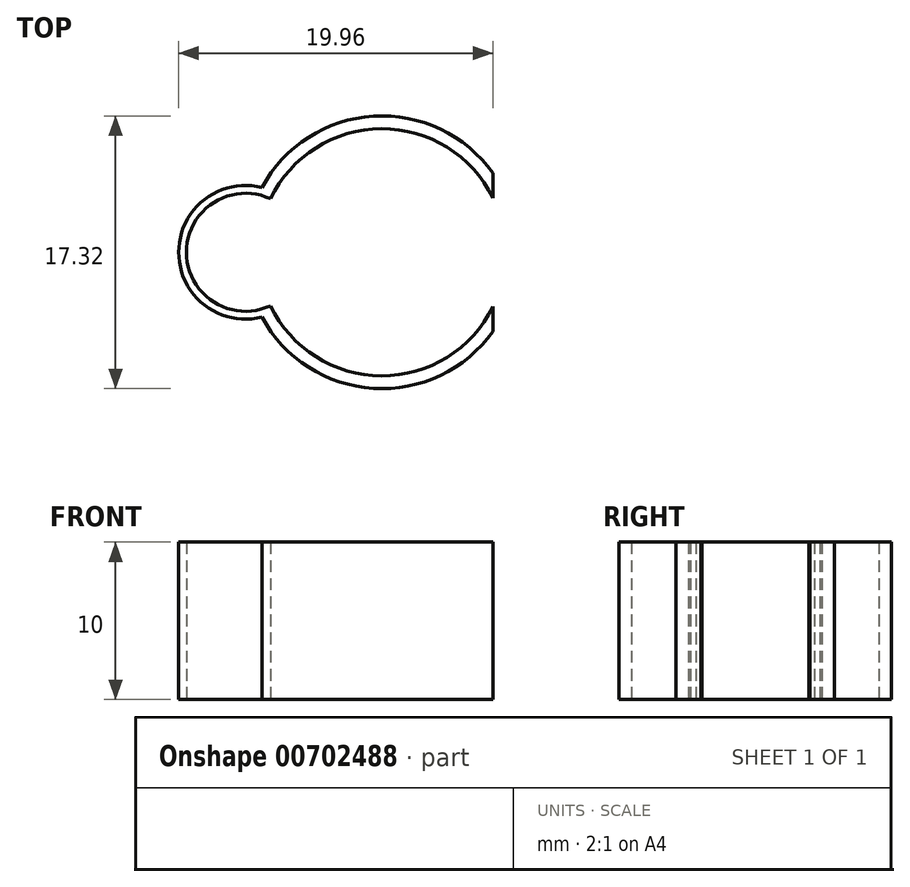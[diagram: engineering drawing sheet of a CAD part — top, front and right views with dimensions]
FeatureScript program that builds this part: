
annotation { "Feature Type Name" : "Feature", "Feature Type Description" : "" }
export const myFeature = defineFeature(function(context is Context, id is Id, definition is map)
    precondition{}
    {
        {
            var Q0;
            Q0=qCreatedBy(makeId("Top.planeOp"),FACE);
            var sketch = newSketch(context, id + "F0", { "sketchPlane" : qUnion([Q0])});
            skCircle(sketch, "E0", {"center": v(0, 0) * mm, "radius": 7.85 * mm});
            skCircle(sketch, "E1", {"center": v(0, 0) * mm, "radius": 8.66 * mm});
            skCircle(sketch, "E2", {"center": v(-8.66, 0) * mm, "radius": 3.75 * mm});
            skCircle(sketch, "E3", {"center": v(-8.66, 0) * mm, "radius": 4.25 * mm});
            skLineSegment(sketch, "E4", {"start": v(7.05, 5.03) * mm, "end": v(7.05, 3.46) * mm});
            skLineSegment(sketch, "E5", {"start": v(7.05, -3.46) * mm, "end": v(7.05, -5.03) * mm});
            skSolve(sketch);
        }
        {
            var Q0;
            {var subQ0=sQuery(id+"F0.wireOp",EDGE,"b5i4uvnI-YS7I-iQm8-zbXG-z9BTK1NYs2xS");Q0=makeQuery(id+"F0.imprint","IMPRINT",FACE,{"disambiguationData":[TD([[makeQuery(id+"F0.imprint","IMPRINT",EDGE,{"derivedFrom":subQ0}),-1.0]])]});}
            var Q1;
            {var subQ0=sQuery(id+"F0.wireOp",EDGE,"E3");var subQ1=sQuery(id+"F0.wireOp",EDGE,"E0");var subQ2=makeQuery(id+"F0.imprint","INTERSECT",VERTEX,{"disambiguationData":[OD(0.0)],"derivedFrom":[subQ1,subQ0]});Q1=makeQuery(id+"F0.imprint","IMPRINT",FACE,{"disambiguationData":[TD([[makeQuery(id+"F0.imprint","IMPRINT",EDGE,{"disambiguationData":[TD([[subQ2,-1.0]])],"derivedFrom":subQ1}),-1.0]])]});}
            var Q2;
            {var subQ0=sQuery(id+"F0.wireOp",EDGE,"MbiijEaS-GBBS-EwlK-B2ir-NtHmAoSLFiy8");Q2=makeQuery(id+"F0.imprint","IMPRINT",FACE,{"disambiguationData":[TD([[makeQuery(id+"F0.imprint","IMPRINT",EDGE,{"derivedFrom":subQ0}),-1.0]])]});}
            var Q3;
            {var subQ0=sQuery(id+"F0.wireOp",EDGE,"E2");var subQ1=sQuery(id+"F0.wireOp",EDGE,"E0");var subQ2=makeQuery(id+"F0.imprint","INTERSECT",VERTEX,{"disambiguationData":[OD(1.0)],"derivedFrom":[subQ1,subQ0]});Q3=makeQuery(id+"F0.imprint","IMPRINT",FACE,{"disambiguationData":[TD([[makeQuery(id+"F0.imprint","IMPRINT",EDGE,{"disambiguationData":[TD([[subQ2,-1.0]])],"derivedFrom":subQ1}),-1.0]])]});}
            var Q4;
            {var subQ0=sQuery(id+"F0.wireOp",EDGE,"E3");var subQ1=sQuery(id+"F0.wireOp",EDGE,"E1");var subQ2=makeQuery(id+"F0.imprint","INTERSECT",VERTEX,{"disambiguationData":[OD(0.0)],"derivedFrom":[subQ1,subQ0]});Q4=makeQuery(id+"F0.imprint","IMPRINT",FACE,{"disambiguationData":[TD([[makeQuery(id+"F0.imprint","IMPRINT",EDGE,{"disambiguationData":[TD([[subQ2,-1.0]])],"derivedFrom":subQ1}),-1.0]])]});}
            extrude(context, id + "F1", {"entities" : qUnion([Q0, Q1, Q2, Q3, Q4]), "depth" : 10 * mm, "offsetDistance" : 25 * mm});
        }
        {
            var Q0;
            Q0=makeQuery(id+"F1.opExtrude","SWEPT_BODY",BODY,{"disambiguationData":[OSD([sQuery(id+"F0.wireOp",EDGE,"E0"),sQuery(id+"F0.wireOp",EDGE,"E1"),sQuery(id+"F0.wireOp",EDGE,"E2"),sQuery(id+"F0.wireOp",EDGE,"E3"),sQuery(id+"F0.wireOp",EDGE,"b5i4uvnI-YS7I-iQm8-zbXG-z9BTK1NYs2xS"),sQuery(id+"F0.wireOp",EDGE,"MbiijEaS-GBBS-EwlK-B2ir-NtHmAoSLFiy8")])]});
            transform(context, id + "F2", {"entities" : qUnion([Q0]), "transformType" : TransformType.TRANSLATION_3D, "dx" : -14.3 * mm, "dy" : 0 * mm, "dz" : 0 * mm, "makeCopy" : true});
        }
        {
            var Q0;
            Q0=makeQuery(id+"F2.opPattern","COPY",BODY,{"derivedFrom":makeQuery(id+"F1.opExtrude","SWEPT_BODY",BODY,{"disambiguationData":[OSD([sQuery(id+"F0.wireOp",EDGE,"E0"),sQuery(id+"F0.wireOp",EDGE,"E1"),sQuery(id+"F0.wireOp",EDGE,"E2"),sQuery(id+"F0.wireOp",EDGE,"E3"),sQuery(id+"F0.wireOp",EDGE,"b5i4uvnI-YS7I-iQm8-zbXG-z9BTK1NYs2xS"),sQuery(id+"F0.wireOp",EDGE,"MbiijEaS-GBBS-EwlK-B2ir-NtHmAoSLFiy8")])]}),"instanceName":"1"});
            transform(context, id + "F3", {"entities" : qUnion([Q0]), "transformType" : TransformType.TRANSLATION_3D, "dx" : -13 * mm, "dy" : 0 * mm, "dz" : 0 * mm, "makeCopy" : true});
        }
        {
            var Q0;
            Q0=makeQuery(id+"F3.opPattern","COPY",BODY,{"derivedFrom":makeQuery(id+"F2.opPattern","COPY",BODY,{"derivedFrom":makeQuery(id+"F1.opExtrude","SWEPT_BODY",BODY,{"disambiguationData":[OSD([sQuery(id+"F0.wireOp",EDGE,"E0"),sQuery(id+"F0.wireOp",EDGE,"E1"),sQuery(id+"F0.wireOp",EDGE,"E2"),sQuery(id+"F0.wireOp",EDGE,"E3"),sQuery(id+"F0.wireOp",EDGE,"b5i4uvnI-YS7I-iQm8-zbXG-z9BTK1NYs2xS"),sQuery(id+"F0.wireOp",EDGE,"MbiijEaS-GBBS-EwlK-B2ir-NtHmAoSLFiy8")])]}),"instanceName":"1"}),"instanceName":"1"});
            deleteBodies(context, id + "F4", {"entities" : qUnion([Q0])});
        }
        {
            var Q0;
            Q0=makeQuery(id+"F2.opPattern","COPY",BODY,{"derivedFrom":makeQuery(id+"F1.opExtrude","SWEPT_BODY",BODY,{"disambiguationData":[OSD([sQuery(id+"F0.wireOp",EDGE,"E0"),sQuery(id+"F0.wireOp",EDGE,"E1"),sQuery(id+"F0.wireOp",EDGE,"E2"),sQuery(id+"F0.wireOp",EDGE,"E3"),sQuery(id+"F0.wireOp",EDGE,"b5i4uvnI-YS7I-iQm8-zbXG-z9BTK1NYs2xS"),sQuery(id+"F0.wireOp",EDGE,"MbiijEaS-GBBS-EwlK-B2ir-NtHmAoSLFiy8")])]}),"instanceName":"1"});
            deleteBodies(context, id + "F5", {"entities" : qUnion([Q0])});
        }
        {
            var Q0;
            {var subQ0=sQuery(id+"F0.wireOp",EDGE,"E4");Q0=makeQuery(id+"F0.imprint","IMPRINT",FACE,{"disambiguationData":[TD([[makeQuery(id+"F0.imprint","IMPRINT",EDGE,{"derivedFrom":subQ0}),-1.0]])]});}
            var Q1;
            {var subQ0=sQuery(id+"F0.wireOp",EDGE,"E5");Q1=makeQuery(id+"F0.imprint","IMPRINT",FACE,{"disambiguationData":[TD([[makeQuery(id+"F0.imprint","IMPRINT",EDGE,{"derivedFrom":subQ0}),-1.0]])]});}
            var Q2;
            {var subQ0=sQuery(id+"F0.wireOp",EDGE,"E3");var subQ1=sQuery(id+"F0.wireOp",EDGE,"E0");var subQ2=makeQuery(id+"F0.imprint","INTERSECT",VERTEX,{"disambiguationData":[OD(0.0)],"derivedFrom":[subQ1,subQ0]});Q2=makeQuery(id+"F0.imprint","IMPRINT",FACE,{"disambiguationData":[TD([[makeQuery(id+"F0.imprint","IMPRINT",EDGE,{"disambiguationData":[TD([[subQ2,-1.0]])],"derivedFrom":subQ1}),-1.0]])]});}
            var Q3;
            {var subQ0=sQuery(id+"F0.wireOp",EDGE,"E2");var subQ1=sQuery(id+"F0.wireOp",EDGE,"E0");var subQ2=makeQuery(id+"F0.imprint","INTERSECT",VERTEX,{"disambiguationData":[OD(1.0)],"derivedFrom":[subQ1,subQ0]});Q3=makeQuery(id+"F0.imprint","IMPRINT",FACE,{"disambiguationData":[TD([[makeQuery(id+"F0.imprint","IMPRINT",EDGE,{"disambiguationData":[TD([[subQ2,-1.0]])],"derivedFrom":subQ1}),-1.0]])]});}
            extrude(context, id + "F6", {"entities" : qUnion([Q0, Q1, Q2, Q3]), "operationType" : NewBodyOperationType.ADD, "depth" : 10 * mm, "offsetDistance" : 25 * mm});
        }
        {
            var Q0;
            Q0=makeQuery(id+"F1.opExtrude","SWEPT_BODY",BODY,{"disambiguationData":[OSD([sQuery(id+"F0.wireOp",EDGE,"E0"),sQuery(id+"F0.wireOp",EDGE,"E2"),sQuery(id+"F0.wireOp",EDGE,"E3")])]});
            transform(context, id + "F7", {"entities" : qUnion([Q0]), "transformType" : TransformType.TRANSLATION_3D, "dx" : -22.5 * mm, "dy" : 0 * mm, "dz" : 0 * mm, "makeCopy" : true});
        }
        {
            var Q0;
            Q0=makeQuery(id+"F1.opExtrude","SWEPT_BODY",BODY,{"disambiguationData":[OSD([sQuery(id+"F0.wireOp",EDGE,"E0"),sQuery(id+"F0.wireOp",EDGE,"E2"),sQuery(id+"F0.wireOp",EDGE,"E3")])]});
            transform(context, id + "F8", {"entities" : qUnion([Q0]), "transformType" : TransformType.TRANSLATION_3D, "dx" : 0 * mm, "dy" : 18.6 * mm, "dz" : 0 * mm, "makeCopy" : true});
        }
        {
            var Q0;
            Q0=makeQuery(id+"F7.opPattern","COPY",BODY,{"derivedFrom":makeQuery(id+"F1.opExtrude","SWEPT_BODY",BODY,{"disambiguationData":[OSD([sQuery(id+"F0.wireOp",EDGE,"E0"),sQuery(id+"F0.wireOp",EDGE,"E2"),sQuery(id+"F0.wireOp",EDGE,"E3")])]}),"instanceName":"1"});
            transform(context, id + "F9", {"entities" : qUnion([Q0]), "transformType" : TransformType.TRANSLATION_3D, "dx" : 0 * mm, "dy" : 20.1 * mm, "dz" : 0 * mm, "makeCopy" : true});
        }
        {
            var Q0;
            Q0=makeQuery(id+"F7.opPattern","COPY",BODY,{"derivedFrom":makeQuery(id+"F1.opExtrude","SWEPT_BODY",BODY,{"disambiguationData":[OSD([sQuery(id+"F0.wireOp",EDGE,"E0"),sQuery(id+"F0.wireOp",EDGE,"E2"),sQuery(id+"F0.wireOp",EDGE,"E3")])]}),"instanceName":"1"});
            transform(context, id + "F10", {"entities" : qUnion([Q0]), "transformType" : TransformType.TRANSLATION_3D, "dx" : 0 * mm, "dy" : -19.2 * mm, "dz" : 0 * mm, "makeCopy" : true});
        }
        {
            var Q0;
            Q0=makeQuery(id+"F1.opExtrude","SWEPT_BODY",BODY,{"disambiguationData":[OSD([sQuery(id+"F0.wireOp",EDGE,"E0"),sQuery(id+"F0.wireOp",EDGE,"E2"),sQuery(id+"F0.wireOp",EDGE,"E3")])]});
            transform(context, id + "F11", {"entities" : qUnion([Q0]), "transformType" : TransformType.TRANSLATION_3D, "dx" : 0 * mm, "dy" : -19.5 * mm, "dz" : 0 * mm, "makeCopy" : true});
        }
        {
            var Q0;
            Q0=makeQuery(id+"F1.opExtrude","SWEPT_BODY",BODY,{"disambiguationData":[OSD([sQuery(id+"F0.wireOp",EDGE,"E0"),sQuery(id+"F0.wireOp",EDGE,"E2"),sQuery(id+"F0.wireOp",EDGE,"E3")])]});
            transform(context, id + "F12", {"entities" : qUnion([Q0]), "transformType" : TransformType.TRANSLATION_3D, "dx" : 25.2 * mm, "dy" : 0 * mm, "dz" : 0 * mm, "makeCopy" : true});
        }
        {
            var Q0;
            Q0=makeQuery(id+"F7.opPattern","COPY",BODY,{"derivedFrom":makeQuery(id+"F1.opExtrude","SWEPT_BODY",BODY,{"disambiguationData":[OSD([sQuery(id+"F0.wireOp",EDGE,"E0"),sQuery(id+"F0.wireOp",EDGE,"E2"),sQuery(id+"F0.wireOp",EDGE,"E3")])]}),"instanceName":"1"});
            var Q1;
            Q1=makeQuery(id+"F8.opPattern","COPY",BODY,{"derivedFrom":makeQuery(id+"F1.opExtrude","SWEPT_BODY",BODY,{"disambiguationData":[OSD([sQuery(id+"F0.wireOp",EDGE,"E0"),sQuery(id+"F0.wireOp",EDGE,"E2"),sQuery(id+"F0.wireOp",EDGE,"E3")])]}),"instanceName":"1"});
            var Q2;
            Q2=makeQuery(id+"F9.opPattern","COPY",BODY,{"derivedFrom":makeQuery(id+"F7.opPattern","COPY",BODY,{"derivedFrom":makeQuery(id+"F1.opExtrude","SWEPT_BODY",BODY,{"disambiguationData":[OSD([sQuery(id+"F0.wireOp",EDGE,"E0"),sQuery(id+"F0.wireOp",EDGE,"E2"),sQuery(id+"F0.wireOp",EDGE,"E3")])]}),"instanceName":"1"}),"instanceName":"1"});
            var Q3;
            Q3=makeQuery(id+"F10.opPattern","COPY",BODY,{"derivedFrom":makeQuery(id+"F7.opPattern","COPY",BODY,{"derivedFrom":makeQuery(id+"F1.opExtrude","SWEPT_BODY",BODY,{"disambiguationData":[OSD([sQuery(id+"F0.wireOp",EDGE,"E0"),sQuery(id+"F0.wireOp",EDGE,"E2"),sQuery(id+"F0.wireOp",EDGE,"E3")])]}),"instanceName":"1"}),"instanceName":"1"});
            var Q4;
            Q4=makeQuery(id+"F11.opPattern","COPY",BODY,{"derivedFrom":makeQuery(id+"F1.opExtrude","SWEPT_BODY",BODY,{"disambiguationData":[OSD([sQuery(id+"F0.wireOp",EDGE,"E0"),sQuery(id+"F0.wireOp",EDGE,"E2"),sQuery(id+"F0.wireOp",EDGE,"E3")])]}),"instanceName":"1"});
            var Q5;
            Q5=makeQuery(id+"F12.opPattern","COPY",BODY,{"derivedFrom":makeQuery(id+"F1.opExtrude","SWEPT_BODY",BODY,{"disambiguationData":[OSD([sQuery(id+"F0.wireOp",EDGE,"E0"),sQuery(id+"F0.wireOp",EDGE,"E2"),sQuery(id+"F0.wireOp",EDGE,"E3")])]}),"instanceName":"1"});
            deleteBodies(context, id + "F13", {"entities" : qUnion([Q0, Q1, Q2, Q3, Q4, Q5])});
        }
    });
